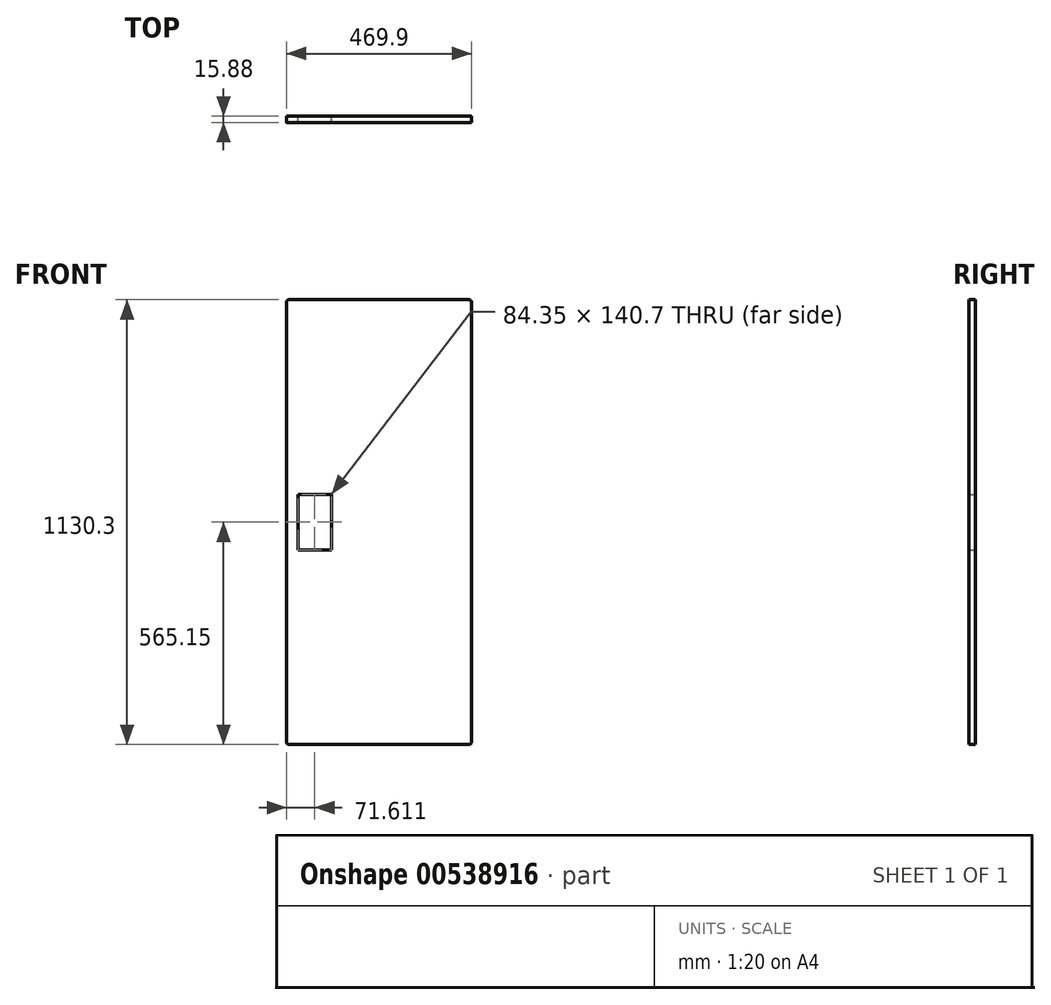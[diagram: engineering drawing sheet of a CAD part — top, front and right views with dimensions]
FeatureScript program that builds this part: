
annotation { "Feature Type Name" : "Feature", "Feature Type Description" : "" }
export const myFeature = defineFeature(function(context is Context, id is Id, definition is map)
    precondition{}
    {
        {
            var Q0;
            Q0=qCreatedBy(makeId("Front.planeOp"),FACE);
            var sketch = newSketch(context, id + "F0", { "sketchPlane" : qUnion([Q0])});
            skLineSegment(sketch, "E0.bottom", {"start": v(228.6, -565.15) * mm, "end": v(-228.6, -565.15) * mm});
            skLineSegment(sketch, "E0.top", {"start": v(228.6, 565.15) * mm, "end": v(-228.6, 565.15) * mm});
            skLineSegment(sketch, "E0.left", {"start": v(234.95, -558.8) * mm, "end": v(234.95, 558.8) * mm});
            skLineSegment(sketch, "E0.right", {"start": v(-234.95, -558.8) * mm, "end": v(-234.95, 558.8) * mm});
            skPoint(sketch, "E0.middle", {"position": v(0, 0) * mm});
            skLineSegment(sketch, "E1.bottom", {"start": v(-121.16, 70.35) * mm, "end": v(-205.51, 70.35) * mm});
            skLineSegment(sketch, "E1.top", {"start": v(-121.16, -70.35) * mm, "end": v(-205.51, -70.35) * mm});
            skLineSegment(sketch, "E1.left", {"start": v(-121.16, 70.35) * mm, "end": v(-121.16, -70.35) * mm});
            skLineSegment(sketch, "E1.right", {"start": v(-205.51, 70.35) * mm, "end": v(-205.51, -70.35) * mm});
            skPoint(sketch, "E1.middle", {"position": v(-163.34, 0) * mm});
            skPoint(sketch, "E2.visualSharp", {"position": v(-234.95, 565.15) * mm});
            skArc(sketch, "E2.filletArc", {"start": v(-228.6, 565.15) * mm, "mid": v(-233.1, 563.3) * mm, "end": v(-234.95, 558.8) * mm});
            skPoint(sketch, "E3.visualSharp", {"position": v(234.95, 565.15) * mm});
            skArc(sketch, "E3.filletArc", {"start": v(234.95, 558.8) * mm, "mid": v(233.1, 563.3) * mm, "end": v(228.6, 565.15) * mm});
            skPoint(sketch, "E4.visualSharp", {"position": v(234.95, -565.15) * mm});
            skArc(sketch, "E4.filletArc", {"start": v(228.6, -565.15) * mm, "mid": v(233.1, -563.3) * mm, "end": v(234.95, -558.8) * mm});
            skPoint(sketch, "E5.visualSharp", {"position": v(-234.95, -565.15) * mm});
            skArc(sketch, "E5.filletArc", {"start": v(-234.95, -558.8) * mm, "mid": v(-233.1, -563.3) * mm, "end": v(-228.6, -565.15) * mm});
            skSolve(sketch);
        }
        {
            var Q0;
            Q0=makeQuery(id+"F0.imprint","IMPRINT",FACE,{"disambiguationData":[TD([[makeQuery(id+"F0.imprint","IMPRINT",EDGE,{"derivedFrom":sQuery(id+"F0.wireOp",EDGE,"E0.bottom")}),-1.0]])]});
            extrude(context, id + "F1", {"entities" : qUnion([Q0]), "depth" : 15.88 * mm, "offsetDistance" : 25.4 * mm});
        }
    });
